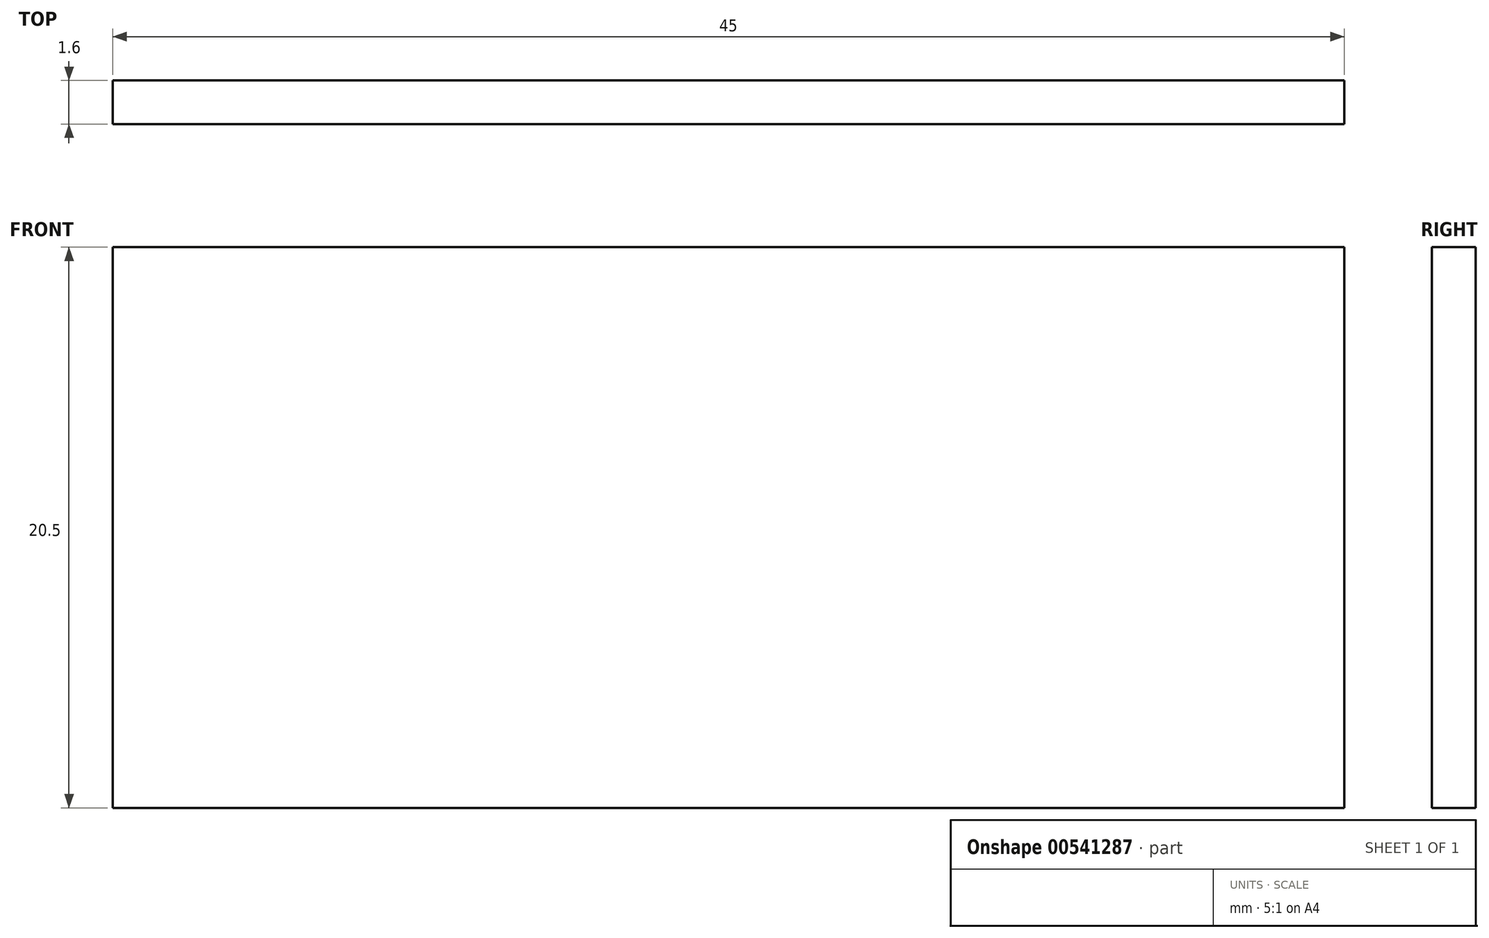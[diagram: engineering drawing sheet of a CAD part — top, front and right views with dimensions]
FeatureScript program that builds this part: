
annotation { "Feature Type Name" : "Feature", "Feature Type Description" : "" }
export const myFeature = defineFeature(function(context is Context, id is Id, definition is map)
    precondition{}
    {
        {
            var Q0;
            Q0=qCreatedBy(makeId("Front.planeOp"),FACE);
            var sketch = newSketch(context, id + "F0", { "sketchPlane" : qUnion([Q0])});
            skLineSegment(sketch, "E0.bottom", {"start": v(22.5, -10.25) * mm, "end": v(-22.5, -10.25) * mm});
            skLineSegment(sketch, "E0.top", {"start": v(22.5, 10.25) * mm, "end": v(-22.5, 10.25) * mm});
            skLineSegment(sketch, "E0.left", {"start": v(22.5, -10.25) * mm, "end": v(22.5, 10.25) * mm});
            skLineSegment(sketch, "E0.right", {"start": v(-22.5, -10.25) * mm, "end": v(-22.5, 10.25) * mm});
            skPoint(sketch, "E0.middle", {"position": v(0, 0) * mm});
            skSolve(sketch);
        }
        {
            var Q0;
            Q0 = qSketchRegion(id + "F0", true);
            extrude(context, id + "F1", {"entities" : qUnion([Q0]), "depth" : 1.6 * mm, "offsetDistance" : 25.4 * mm});
        }
        {
            var Q0;
            Q0=makeQuery(id+"F1.opExtrude","CAP_FACE",FACE,{"disambiguationData":[OSD([sQuery(id+"F0.wireOp",EDGE,"E0.bottom"),sQuery(id+"F0.wireOp",EDGE,"E0.top"),sQuery(id+"F0.wireOp",EDGE,"E0.left"),sQuery(id+"F0.wireOp",EDGE,"E0.right")])],"isStart":false});
            var sketch = newSketch(context, id + "F2", { "sketchPlane" : qUnion([Q0])});
            skCircle(sketch, "E1", {"center": v(-13.5, 0) * mm, "radius": 8 * mm});
            skCircle(sketch, "E2", {"center": v(13.5, 0) * mm, "radius": 8 * mm});
            skLineSegment(sketch, "E3", {"start": v(0, 10.25) * mm, "end": v(0, -10.25) * mm});
            skLineSegment(sketch, "E4", {"start": v(-5.5, 0) * mm, "end": v(5.5, 0) * mm});
            skPoint(sketch, "E5", {"position": v(0, 0) * mm});
            skSolve(sketch);
        }
        {
            var Q0;
            Q0=sQuery(id+"F2.wireOp",EDGE,"E1");
            var Q1;
            Q1=sQuery(id+"F2.wireOp",EDGE,"E2");
            extrude(context, id + "F3", {"bodyType" : ToolBodyType.SURFACE, "surfaceEntities" : qUnion([Q0, Q1]), "depth" : 12 * mm, "offsetDistance" : 25.4 * mm});
        }
    });
